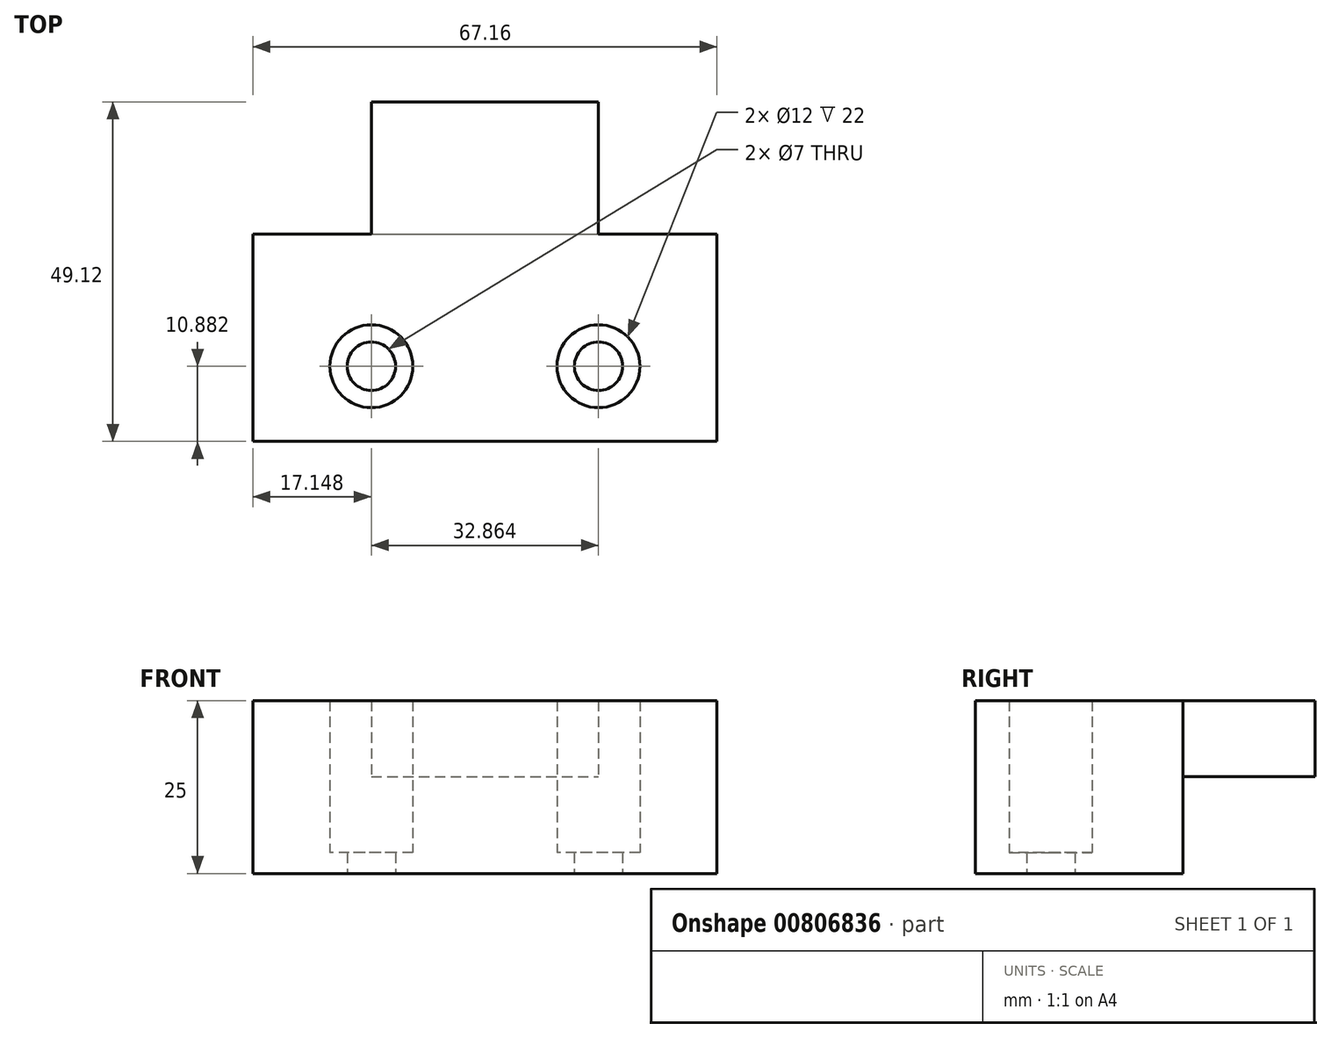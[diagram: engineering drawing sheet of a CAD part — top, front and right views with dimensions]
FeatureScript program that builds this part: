
annotation { "Feature Type Name" : "Feature", "Feature Type Description" : "" }
export const myFeature = defineFeature(function(context is Context, id is Id, definition is map)
    precondition{}
    {
        {
            var Q0;
            Q0=qCreatedBy(makeId("Top.planeOp"),FACE);
            var sketch = newSketch(context, id + "F0", { "sketchPlane" : qUnion([Q0])});
            skLineSegment(sketch, "E0.bottom", {"start": v(33.58, 30) * mm, "end": v(-33.58, 30) * mm});
            skLineSegment(sketch, "E0.top", {"start": v(33.58, -30) * mm, "end": v(-33.58, -30) * mm});
            skLineSegment(sketch, "E0.left", {"start": v(33.58, 30) * mm, "end": v(33.58, -30) * mm});
            skLineSegment(sketch, "E0.right", {"start": v(-33.58, 30) * mm, "end": v(-33.58, -30) * mm});
            skPoint(sketch, "E0.middle", {"position": v(0, 0) * mm});
            skLineSegment(sketch, "E1.bottom", {"start": v(-33.58, 30) * mm, "end": v(33.58, 30) * mm});
            skLineSegment(sketch, "E1.top", {"start": v(-33.58, 0) * mm, "end": v(33.58, 0) * mm});
            skLineSegment(sketch, "E1.left", {"start": v(-33.58, 30) * mm, "end": v(-33.58, 0) * mm});
            skLineSegment(sketch, "E1.right", {"start": v(33.58, 30) * mm, "end": v(33.58, 0) * mm});
            skLineSegment(sketch, "E2.bottom", {"start": v(16.43, -19.12) * mm, "end": v(-16.43, -19.12) * mm});
            skLineSegment(sketch, "E2.top", {"start": v(16.43, 19.12) * mm, "end": v(-16.43, 19.12) * mm});
            skLineSegment(sketch, "E2.left", {"start": v(16.43, -19.12) * mm, "end": v(16.43, 19.12) * mm});
            skLineSegment(sketch, "E2.right", {"start": v(-16.43, -19.12) * mm, "end": v(-16.43, 19.12) * mm});
            skCircle(sketch, "E3", {"center": v(16.43, -19.12) * mm, "radius": 6 * mm});
            skCircle(sketch, "E4", {"center": v(-16.43, -19.12) * mm, "radius": 6 * mm});
            skCircle(sketch, "E5", {"center": v(-16.43, -19.12) * mm, "radius": 3.5 * mm});
            skCircle(sketch, "E6", {"center": v(16.43, -19.12) * mm, "radius": 3.5 * mm});
            skSolve(sketch);
        }
        {
            var Q0;
            Q0=makeQuery(id+"F0.imprint","IMPRINT",FACE,{"disambiguationData":[TD([[makeQuery(id+"F0.imprint","IMPRINT",EDGE,{"derivedFrom":sQuery(id+"F0.wireOp",EDGE,"E1.bottom")}),-1.0]])]});
            var Q1;
            {var subQ5=sQuery(id+"F0.wireOp",EDGE,"E2.top");Q1=makeQuery(id+"F0.imprint","IMPRINT",FACE,{"disambiguationData":[TD([[makeQuery(id+"F0.imprint","IMPRINT",EDGE,{"derivedFrom":subQ5}),1.0]])]});}
            var Q2;
            {var subQ1=sQuery(id+"F0.wireOp",EDGE,"E1.top");var subQ5=sQuery(id+"F0.wireOp",EDGE,"E2.right");var subQ6=makeQuery(id+"F0.imprint","INTERSECT",VERTEX,{"derivedFrom":[subQ1,subQ5]});Q2=makeQuery(id+"F0.imprint","IMPRINT",FACE,{"disambiguationData":[TD([[makeQuery(id+"F0.imprint","IMPRINT",EDGE,{"disambiguationData":[TD([[subQ6,-1.0]])],"derivedFrom":subQ1}),-1.0]])]});}
            var Q3;
            Q3=makeQuery(id+"F0.imprint","IMPRINT",FACE,{"disambiguationData":[TD([[makeQuery(id+"F0.imprint","IMPRINT",EDGE,{"derivedFrom":sQuery(id+"F0.wireOp",EDGE,"E0.top")}),-1.0]])]});
            extrude(context, id + "F1", {"entities" : qUnion([Q0, Q1, Q2, Q3]), "depth" : 25 * mm, "offsetDistance" : 25 * mm});
        }
        {
            var Q0;
            {var subQ0=sQuery(id+"F0.wireOp",EDGE,"E4");var subQ1=sQuery(id+"F0.wireOp",EDGE,"E2.bottom");var subQ2=makeQuery(id+"F0.imprint","INTERSECT",VERTEX,{"derivedFrom":[subQ1,subQ0]});Q0=makeQuery(id+"F0.imprint","IMPRINT",FACE,{"disambiguationData":[TD([[makeQuery(id+"F0.imprint","IMPRINT",EDGE,{"disambiguationData":[TD([[subQ2,-1.0]])],"derivedFrom":subQ1}),1.0]])]});}
            var Q1;
            {var subQ0=sQuery(id+"F0.wireOp",EDGE,"E4");var subQ1=sQuery(id+"F0.wireOp",EDGE,"E2.bottom");var subQ2=makeQuery(id+"F0.imprint","INTERSECT",VERTEX,{"derivedFrom":[subQ1,subQ0]});Q1=makeQuery(id+"F0.imprint","IMPRINT",FACE,{"disambiguationData":[TD([[makeQuery(id+"F0.imprint","IMPRINT",EDGE,{"disambiguationData":[TD([[subQ2,-1.0]])],"derivedFrom":subQ1}),-1.0]])]});}
            var Q2;
            {var subQ0=sQuery(id+"F0.wireOp",EDGE,"E6");var subQ1=sQuery(id+"F0.wireOp",EDGE,"E2.bottom");var subQ2=makeQuery(id+"F0.imprint","INTERSECT",VERTEX,{"derivedFrom":[subQ1,subQ0]});Q2=makeQuery(id+"F0.imprint","IMPRINT",FACE,{"disambiguationData":[TD([[makeQuery(id+"F0.imprint","IMPRINT",EDGE,{"disambiguationData":[TD([[subQ2,-1.0]])],"derivedFrom":subQ1}),-1.0]])]});}
            var Q3;
            {var subQ0=sQuery(id+"F0.wireOp",EDGE,"E6");var subQ1=sQuery(id+"F0.wireOp",EDGE,"E2.bottom");var subQ2=makeQuery(id+"F0.imprint","INTERSECT",VERTEX,{"derivedFrom":[subQ1,subQ0]});Q3=makeQuery(id+"F0.imprint","IMPRINT",FACE,{"disambiguationData":[TD([[makeQuery(id+"F0.imprint","IMPRINT",EDGE,{"disambiguationData":[TD([[subQ2,-1.0]])],"derivedFrom":subQ1}),1.0]])]});}
            extrude(context, id + "F2", {"entities" : qUnion([Q0, Q1, Q2, Q3]), "operationType" : NewBodyOperationType.ADD, "depth" : 3 * mm, "offsetDistance" : 25 * mm});
        }
        {
            var Q0;
            Q0=makeQuery(id+"F0.imprint","IMPRINT",FACE,{"disambiguationData":[TD([[makeQuery(id+"F0.imprint","IMPRINT",EDGE,{"derivedFrom":sQuery(id+"F0.wireOp",EDGE,"E1.bottom")}),-1.0]])]});
            var Q1;
            {var subQ5=sQuery(id+"F0.wireOp",EDGE,"E2.top");Q1=makeQuery(id+"F0.imprint","IMPRINT",FACE,{"disambiguationData":[TD([[makeQuery(id+"F0.imprint","IMPRINT",EDGE,{"derivedFrom":subQ5}),1.0]])]});}
            extrude(context, id + "F3", {"entities" : qUnion([Q0, Q1]), "operationType" : NewBodyOperationType.REMOVE, "oppositeDirection" : true, "depth" : -14 * mm, "offsetDistance" : 25 * mm});
        }
    });
